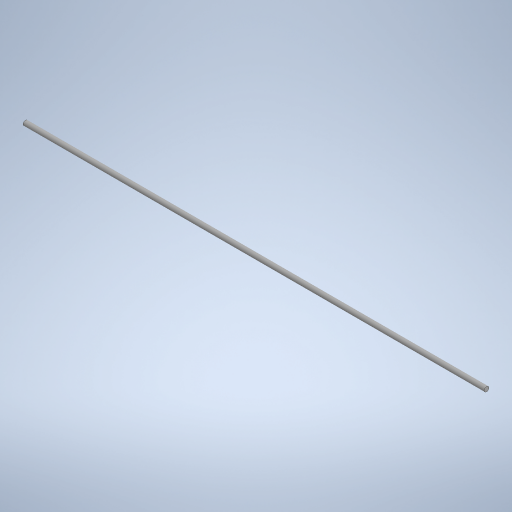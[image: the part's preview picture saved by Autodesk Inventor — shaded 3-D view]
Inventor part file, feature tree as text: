
AUTODESK INVENTOR PART (.ipt)
format: ipt  version: 2024 (Build 280153000, 153)  size: 236,032 bytes
history: native  units: in
note: dims shown in document units (in); Inventor stores cm internally (conversion verified against a paired STEP export)
features: extrude x1, sketch x1
ambient origin geometry x8: Origin, YZ Plane, XZ Plane, XY Plane, X Axis, Y Axis, Z Axis, Center Point
bodies: Solid1 (feature_tree)
feature tree (2):
  extrude  "Extrusion1"  Depth=12.0in TaperAngle=0.0deg
  sketch  "Sketch1"  dims[d0=0.125in d1=12.0in d2=0.0in]
